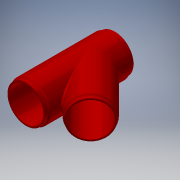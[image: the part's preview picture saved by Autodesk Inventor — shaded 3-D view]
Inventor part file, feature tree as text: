
AUTODESK INVENTOR PART (.ipt)
format: ipt  version: 2017.3 (Build 213257000, 257)  size: 329,728 bytes
history: native  units: in
note: dims shown in document units (in); Inventor stores cm internally (conversion verified against a paired STEP export)
features: extrude x18, sketch x14, fillet x6, chamfer x3, plane x1
ambient origin geometry x8: Origin, YZ Plane, XZ Plane, XY Plane, X Axis, Y Axis, Z Axis, Center Point
bodies: Solid1 (feature_tree)
feature tree (42):
  sketch  "Sketch1"  dims[d0=28.5in d1=31.0in]
  extrude  "Extrusion1"  Depth=31.0in
  plane  "Work Plane1"
  sketch  "Sketch2"  dims[d2=33.0in d3=52.9606in d4=19.4961in d5=0.0in d6=0.0in]
  extrude  "Extrusion2"  Depth=52.9606in TaperAngle=0.0deg
  extrude  "Extrusion3"  Depth=28.5in
  extrude  "Extrusion4"  Depth=33.0in
  extrude  "Extrusion5"  Depth=30.0in
  extrude  "Extrusion6"  Depth=30.0in
  extrude  "Extrusion7"  TaperAngle=0.0deg  [1 undecoded]
  extrude  "Extrusion8"  Depth=0.5in
  extrude  "Extrusion9"  Depth=49.9606in
  fillet  "Fillet1"  Radius=16.4961in
  fillet  "Fillet2"  [1 undecoded]
  fillet  "Fillet3"  Radius=49.9606in
  fillet  "Fillet4"  [1 undecoded]
  extrude  "Extrusion10"  TaperAngle=0.0deg  [1 undecoded]
  extrude  "Extrusion11"  TaperAngle=0.0deg  [1 undecoded]
  extrude  "Extrusion12"  Depth=6.0in
  fillet  "Fillet5"  Radius=1.0in
  chamfer  "Chamfer2"  Distance=1.0in
  fillet  "Fillet6"  Radius=32.48in
  chamfer  "Chamfer3"  Distance=1.0in
  extrude  "Extrusion13"  Depth=32.48in
  extrude  "Extrusion14"  Depth=1.0in TaperAngle=0.0deg
  extrude  "Extrusion15"  Depth=0.0312in
  chamfer  "Chamfer4"  Distance=0.74in
  extrude  "Extrusion16"  Depth=0.125in TaperAngle=45.0deg
  extrude  "Extrusion17"  Depth=0.0312in
  extrude  "Extrusion18"  Depth=0.0312in TaperAngle=45.0deg
  sketch  "Sketch3"  dims[d7=45.0deg d8=28.5in]
  sketch  "Sketch4"  dims[d9=31.0in d10=33.0in]
  sketch  "Sketch5"  dims[d11=52.9606in d12=0.0in d13=30.0in]
  sketch  "Sketch6"  dims[d14=0.5in d15=0.0in d16=30.0in]
  sketch  "Sketch7"  dims[d17=0.5in d18=0.0in]
  sketch  "Sketch8"  dims[d19=30.0in d20=0.5in]
  sketch  "Sketch9"  dims[d21=0.0in d22=49.9606in d23=16.4961in d24=0.0in d25=0.0in d26=49.9606in d27=0.0in]
  sketch  "Sketch10"  dims[d28=52.9606in d29=0.0in]
  sketch  "Sketch11"  dims[d30=52.9606in d31=0.0in]
  sketch  "Sketch12"  dims[d32=1.0in d33=6.0in d34=1.0in]
  sketch  "Sketch13"  dims[d35=1.0in]
  sketch  "Sketch14"  dims[d39=32.48in d40=1.0in d41=0.0in d42=32.48in d43=1.0in d44=0.0in d45=32.48in d46=1.0in d47=0.0in d48=0.0312in d49=0.74in d50=0.125in d51=45.0deg d52=0.0312in d53=0.0312in d54=0.125in d55=45.0deg d56=1.0in d57=0.0in d58=1.0in d59=0.0in d60=1.0in d61=0.0in d62=0.26in d64=0.125in d65=45.0deg d66=1.0in d67=0.0in d68=1.0in d69=0.0in d70=1.0in d71=0.0in]
note: 5 required parameter values undecoded (feature->parameter linkage not recoverable at this tier; creation-order binding heuristic only, values carry confidence <= 0.55)
